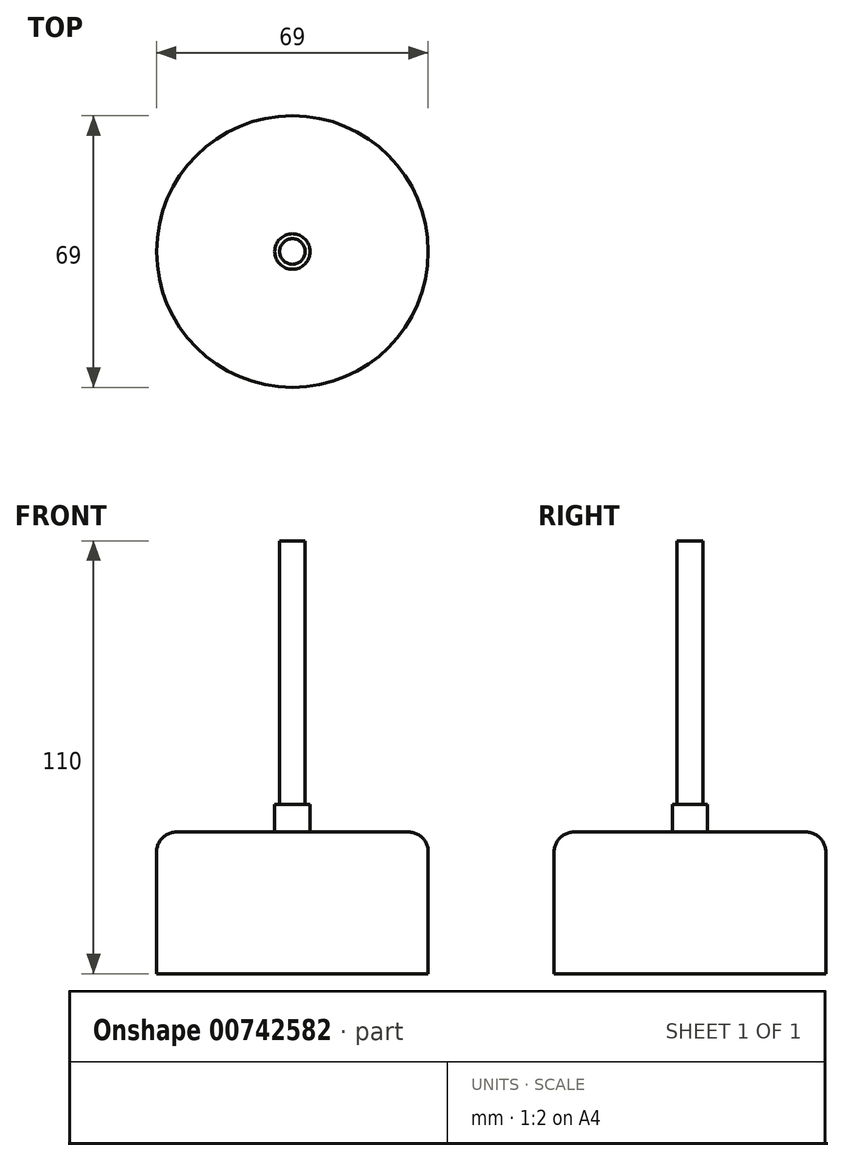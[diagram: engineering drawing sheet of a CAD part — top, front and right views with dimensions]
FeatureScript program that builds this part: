
annotation { "Feature Type Name" : "Feature", "Feature Type Description" : "" }
export const myFeature = defineFeature(function(context is Context, id is Id, definition is map)
    precondition{}
    {
        {
            var Q0;
            Q0=qCreatedBy(makeId("Top.planeOp"),FACE);
            var sketch = newSketch(context, id + "F0", { "sketchPlane" : qUnion([Q0])});
            skCircle(sketch, "E0", {"center": v(0, 0) * mm, "radius": 34.5 * mm});
            skSolve(sketch);
        }
        {
            var Q0;
            Q0=qCreatedBy(makeId("Top.planeOp"),FACE);
            var sketch = newSketch(context, id + "F1", { "sketchPlane" : qUnion([Q0])});
            skCircle(sketch, "E1", {"center": v(0, 0) * mm, "radius": 3.25 * mm});
            skSolve(sketch);
        }
        {
            var Q0;
            Q0=qCreatedBy(makeId("Top.planeOp"),FACE);
            var sketch = newSketch(context, id + "F2", { "sketchPlane" : qUnion([Q0])});
            skCircle(sketch, "E2", {"center": v(0, 0) * mm, "radius": 4.5 * mm});
            skSolve(sketch);
        }
        {
            var Q0;
            Q0 = qSketchRegion(id + "F1", true);
            extrude(context, id + "F3", {"entities" : qUnion([Q0]), "depth" : 110 * mm, "offsetDistance" : 25 * mm});
        }
        {
            var Q0;
            Q0=makeQuery(id+"F0.imprint","IMPRINT",FACE,{"disambiguationData":[TD([[makeQuery(id+"F0.imprint","IMPRINT",EDGE,{"derivedFrom":sQuery(id+"F0.wireOp",EDGE,"E0")}),1.0]])]});
            extrude(context, id + "F4", {"entities" : qUnion([Q0]), "operationType" : NewBodyOperationType.ADD, "depth" : 36 * mm, "offsetDistance" : 25 * mm});
        }
        {
            var Q0;
            Q0 = qSketchRegion(id + "F2", true);
            extrude(context, id + "F5", {"entities" : qUnion([Q0]), "operationType" : NewBodyOperationType.ADD, "depth" : 43 * mm, "offsetDistance" : 25 * mm});
        }
        {
            var Q0;
            Q0=makeQuery(id+"F4.opExtrude","CAP_EDGE",EDGE,{"disambiguationData":[OSD([sQuery(id+"F0.wireOp",EDGE,"E0")])],"isStart":false});
            fillet(context, id + "F6", {"entities" : qUnion([Q0]), "radius" : 5 * mm, "tangentPropagation" : true, "allowEdgeOverflow" : false});
        }
    });
